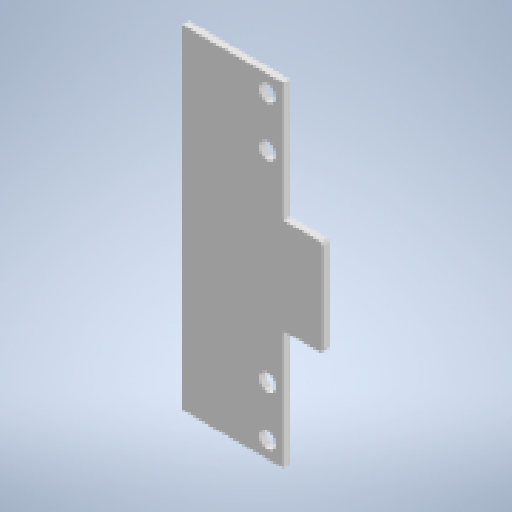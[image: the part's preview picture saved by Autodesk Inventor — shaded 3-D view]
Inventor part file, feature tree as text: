
AUTODESK INVENTOR PART (.ipt)
format: ipt  version: 2025 (Build 290162010, 162A)  size: 176,128 bytes
history: native  units: mm
features: sketch x2, sheet_metal_op x1, hole x1, fillet x1, other x1, projected_geometry x1
ambient origin geometry x8: Origin, YZ Plane, XZ Plane, XY Plane, X Axis, Y Axis, Z Axis, Center Point
bodies: Solid1 (feature_tree)
feature tree (7):
  sheet_metal_op  "Face1"
  hole  "Hole1"  [1 undecoded]
  fillet  "Fillet1"  Radius=112.0mm
  sketch  "Sketch1"  dims[d2=8.0mm]
  other  "Plate1"
  sketch  "Sketch2"  dims[d3=20.0mm d4=6.0mm d5=4.0mm d6=2.0mm d7=90.0deg d8=8.0mm d9=20.594885mm d16=112.0mm d17=400.0mm d19=20.0mm d20=20.0mm d21=360.0mm d22=120.0mm d23=120.0mm d24=47.0mm d25=115.0mm d26=4.0mm]
  projected_geometry  "Projected Loop1"
note: 1 required parameter value undecoded (feature->parameter linkage not recoverable at this tier; creation-order binding heuristic only, values carry confidence <= 0.55)
